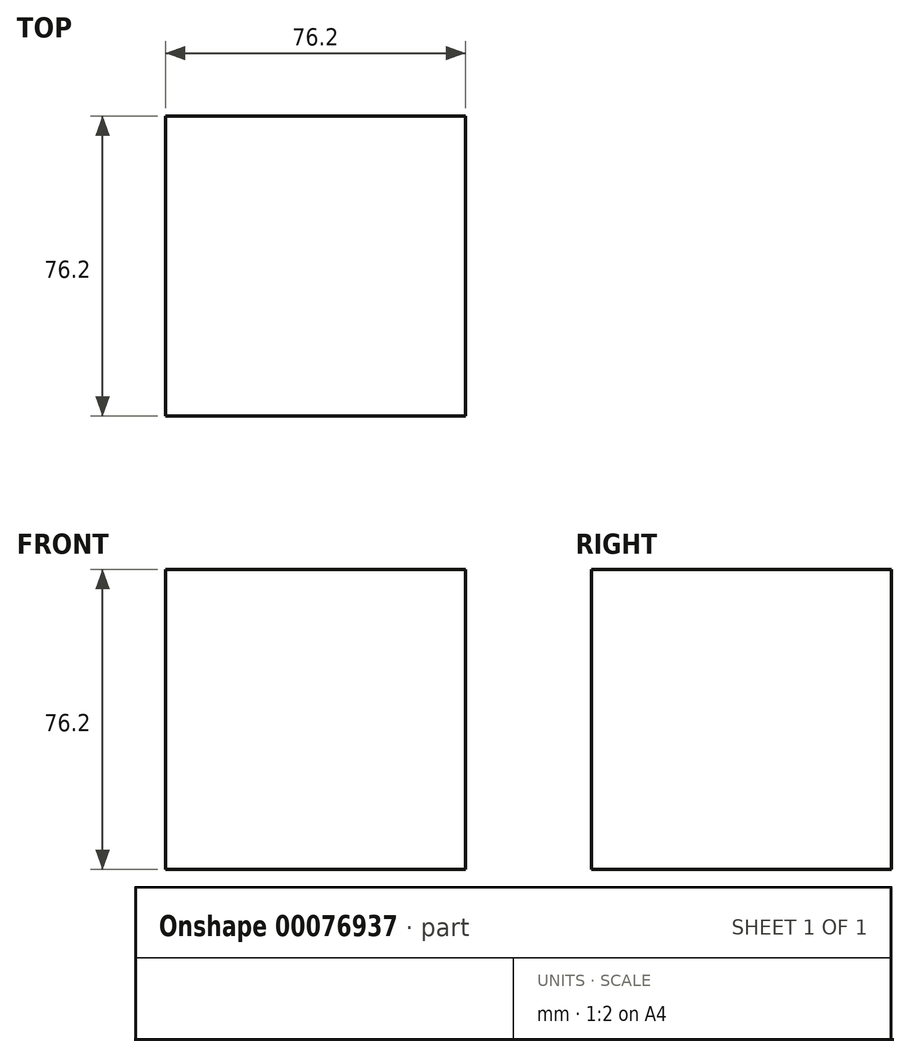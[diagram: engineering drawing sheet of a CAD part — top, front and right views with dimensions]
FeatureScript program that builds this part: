
annotation { "Feature Type Name" : "Feature", "Feature Type Description" : "" }
export const myFeature = defineFeature(function(context is Context, id is Id, definition is map)
    precondition{}
    {
        {
            var Q0;
            Q0=qCreatedBy(makeId("Top.planeOp"),FACE);
            var sketch = newSketch(context, id + "F0", { "sketchPlane" : qUnion([Q0])});
            skLineSegment(sketch, "E0.bottom", {"start": v(38.1, -38.1) * mm, "end": v(-38.1, -38.1) * mm});
            skLineSegment(sketch, "E0.top", {"start": v(38.1, 38.1) * mm, "end": v(-38.1, 38.1) * mm});
            skLineSegment(sketch, "E0.left", {"start": v(38.1, -38.1) * mm, "end": v(38.1, 38.1) * mm});
            skLineSegment(sketch, "E0.right", {"start": v(-38.1, -38.1) * mm, "end": v(-38.1, 38.1) * mm});
            skPoint(sketch, "E0.middle", {"position": v(0, 0) * mm});
            skSolve(sketch);
        }
        {
            var Q0;
            Q0=makeQuery(id+"F0.imprint","IMPRINT",FACE,{"disambiguationData":[TD([[makeQuery(id+"F0.imprint","IMPRINT",EDGE,{"derivedFrom":sQuery(id+"F0.wireOp",EDGE,"E0.bottom")}),-1.0]])]});
            extrude(context, id + "F1", {"entities" : qUnion([Q0]), "depth" : 76.2 * mm});
        }
    });
